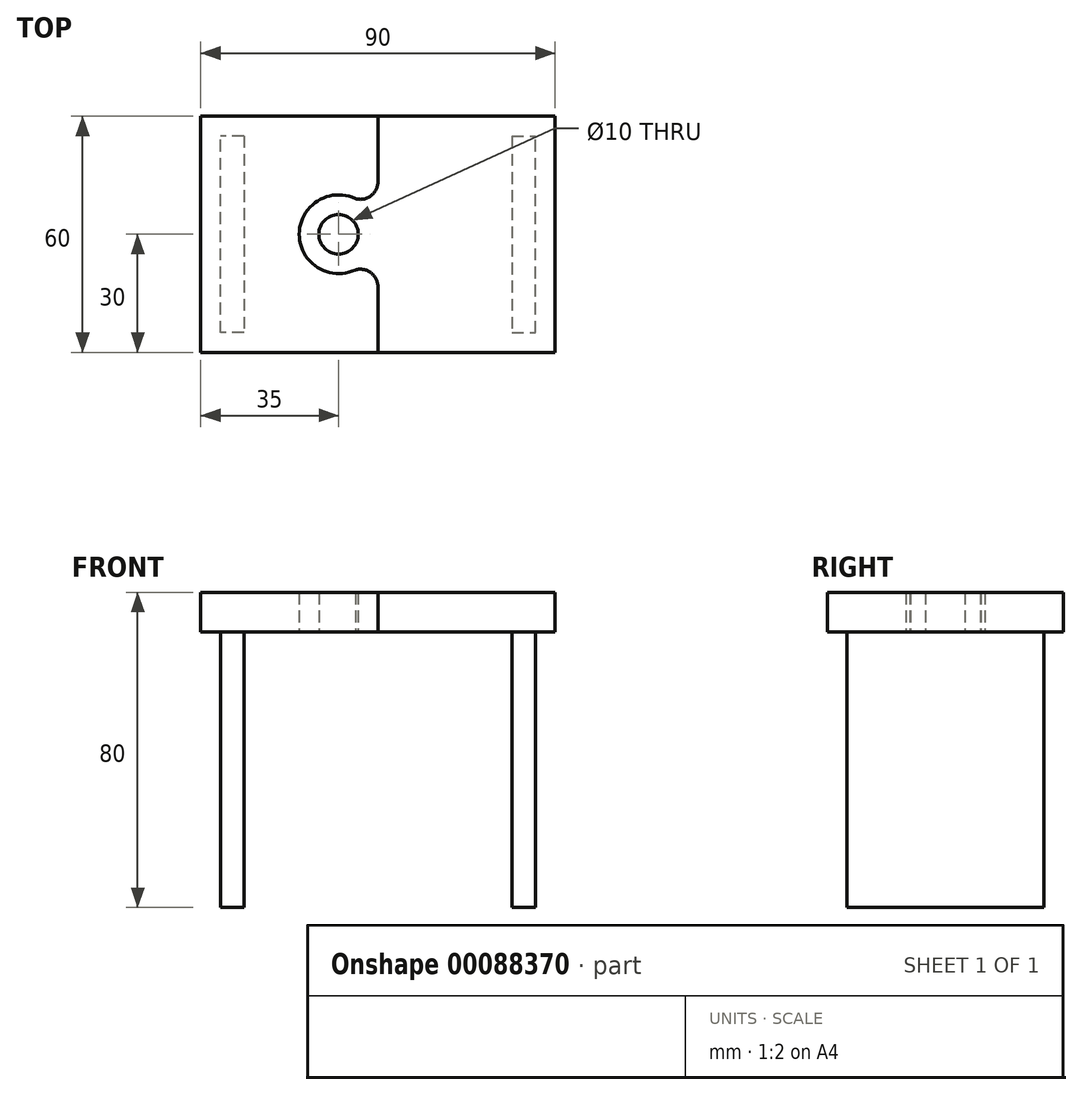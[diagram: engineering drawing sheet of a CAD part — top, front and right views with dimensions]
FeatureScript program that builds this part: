
annotation { "Feature Type Name" : "Feature", "Feature Type Description" : "" }
export const myFeature = defineFeature(function(context is Context, id is Id, definition is map)
    precondition{}
    {
        {
            var Q0;
            Q0=qCreatedBy(makeId("Top.planeOp"),FACE);
            var sketch = newSketch(context, id + "F0", { "sketchPlane" : qUnion([Q0])});
            skLineSegment(sketch, "E0", {"start": v(0, 0) * mm, "end": v(45, 0) * mm});
            skLineSegment(sketch, "E1", {"start": v(45, 60) * mm, "end": v(0, 60) * mm});
            skLineSegment(sketch, "E2", {"start": v(0, 60) * mm, "end": v(0, 0) * mm});
            skArc(sketch, "E3", {"start": v(39.25, 39.05) * mm, "mid": v(25, 30) * mm, "end": v(39.25, 20.95) * mm});
            skLineSegment(sketch, "E4", {"start": v(35, 60) * mm, "end": v(35, 0) * mm, "construction": true});
            skLineSegment(sketch, "E5", {"start": v(45, 0) * mm, "end": v(45, 16.63) * mm});
            skArc(sketch, "E6", {"start": v(45, 16.63) * mm, "mid": v(43.2, 20.22) * mm, "end": v(39.25, 20.95) * mm});
            skLineSegment(sketch, "E7", {"start": v(-9.3, 30) * mm, "end": v(56.7, 30) * mm, "construction": true});
            skArc(sketch, "E8.MirrorCS", {"start": v(45, 43.37) * mm, "mid": v(43.2, 39.78) * mm, "end": v(39.25, 39.05) * mm});
            skLineSegment(sketch, "E9.MirrorCS", {"start": v(45, 60) * mm, "end": v(45, 43.37) * mm});
            skLineSegment(sketch, "E10", {"start": v(25, 27.43) * mm, "end": v(25, 30) * mm, "construction": true});
            skSolve(sketch);
        }
        {
            var Q0;
            Q0 = qSketchRegion(id + "F0", true);
            extrude(context, id + "F1", {"entities" : qUnion([Q0]), "depth" : 10 * mm});
        }
        {
            var Q0;
            Q0=qCreatedBy(makeId("Top.planeOp"),FACE);
            var sketch = newSketch(context, id + "F2", { "sketchPlane" : qUnion([Q0])});
            skArc(sketch, "E11", {"start": v(39.25, 39.05) * mm, "mid": v(25, 30) * mm, "end": v(39.25, 20.95) * mm});
            skArc(sketch, "E12", {"start": v(38.34, 39.42) * mm, "mid": v(42.8, 39.5) * mm, "end": v(45, 43.37) * mm});
            skLineSegment(sketch, "E13", {"start": v(35, 30) * mm, "end": v(-8.78, 30) * mm, "construction": true});
            skArc(sketch, "E14.MirrorCS", {"start": v(38.34, 20.58) * mm, "mid": v(42.8, 20.5) * mm, "end": v(45, 16.63) * mm});
            skLineSegment(sketch, "E15", {"start": v(45, 16.63) * mm, "end": v(45, 0) * mm});
            skLineSegment(sketch, "E16", {"start": v(45, 0) * mm, "end": v(90, 0) * mm});
            skLineSegment(sketch, "E17", {"start": v(90, 0) * mm, "end": v(90, 60) * mm});
            skLineSegment(sketch, "E18", {"start": v(90, 60) * mm, "end": v(45, 60) * mm});
            skLineSegment(sketch, "E19", {"start": v(45, 60) * mm, "end": v(45, 43.37) * mm});
            skCircle(sketch, "E20", {"center": v(35, 30) * mm, "radius": 5 * mm});
            skSolve(sketch);
        }
        {
            var Q0;
            Q0 = qSketchRegion(id + "F2", true);
            extrude(context, id + "F3", {"entities" : qUnion([Q0]), "depth" : 10 * mm});
        }
        {
            var Q0;
            Q0=qCreatedBy(makeId("Top.planeOp"),FACE);
            var sketch = newSketch(context, id + "F4", { "sketchPlane" : qUnion([Q0])});
            skLineSegment(sketch, "E21", {"start": v(0, 55) * mm, "end": v(5, 55) * mm, "construction": true});
            skLineSegment(sketch, "E22", {"start": v(5, 55) * mm, "end": v(5, 60) * mm, "construction": true});
            skLineSegment(sketch, "E23.bottom", {"start": v(0, 0) * mm, "end": v(5, 0) * mm, "construction": true});
            skLineSegment(sketch, "E23.top", {"start": v(0, 5) * mm, "end": v(5, 5) * mm, "construction": true});
            skLineSegment(sketch, "E23.left", {"start": v(0, 0) * mm, "end": v(0, 5) * mm, "construction": true});
            skLineSegment(sketch, "E23.right", {"start": v(5, 0) * mm, "end": v(5, 5) * mm, "construction": true});
            skLineSegment(sketch, "E24.bottom", {"start": v(5, 5) * mm, "end": v(5, 5) * mm});
            skLineSegment(sketch, "E24.top", {"start": v(5, 55) * mm, "end": v(5, 55) * mm});
            skLineSegment(sketch, "E25.left", {"start": v(5, 5) * mm, "end": v(5, 55) * mm});
            skLineSegment(sketch, "E25.right", {"start": v(5, 5) * mm, "end": v(5, 55) * mm});
            skLineSegment(sketch, "E26.bottom", {"start": v(11, 55) * mm, "end": v(5, 55) * mm});
            skLineSegment(sketch, "E26.top", {"start": v(11, 5) * mm, "end": v(5, 5) * mm});
            skLineSegment(sketch, "E26.left", {"start": v(11, 55) * mm, "end": v(11, 5) * mm});
            skLineSegment(sketch, "E26.right", {"start": v(5, 55) * mm, "end": v(5, 5) * mm});
            skLineSegment(sketch, "E27.MirrorCS", {"start": v(85, 5) * mm, "end": v(85, 55) * mm});
            skLineSegment(sketch, "E28.MirrorCS", {"start": v(85, 5) * mm, "end": v(85, 5) * mm});
            skLineSegment(sketch, "E29.MirrorCS", {"start": v(85, 55) * mm, "end": v(85, 55) * mm});
            skLineSegment(sketch, "E30.MirrorCS", {"start": v(85, 55) * mm, "end": v(85, 5) * mm});
            skLineSegment(sketch, "E31.MirrorCS", {"start": v(79, 55) * mm, "end": v(79, 5) * mm});
            skLineSegment(sketch, "E32.MirrorCS", {"start": v(79, 5) * mm, "end": v(85, 5) * mm});
            skLineSegment(sketch, "E33.MirrorCS", {"start": v(79, 55) * mm, "end": v(85, 55) * mm});
            skLineSegment(sketch, "E34.MirrorCS", {"start": v(85, 0) * mm, "end": v(85, 5) * mm, "construction": true});
            skLineSegment(sketch, "E35.MirrorCS", {"start": v(90, 5) * mm, "end": v(85, 5) * mm, "construction": true});
            skLineSegment(sketch, "E36.MirrorCS", {"start": v(85, 55) * mm, "end": v(85, 60) * mm, "construction": true});
            skLineSegment(sketch, "E37.MirrorCS", {"start": v(90, 55) * mm, "end": v(85, 55) * mm, "construction": true});
            skSolve(sketch);
        }
        {
            var Q0;
            Q0 = qSketchRegion(id + "F4", true);
            extrude(context, id + "F5", {"entities" : qUnion([Q0]), "oppositeDirection" : true, "depth" : 70 * mm});
        }
    });
